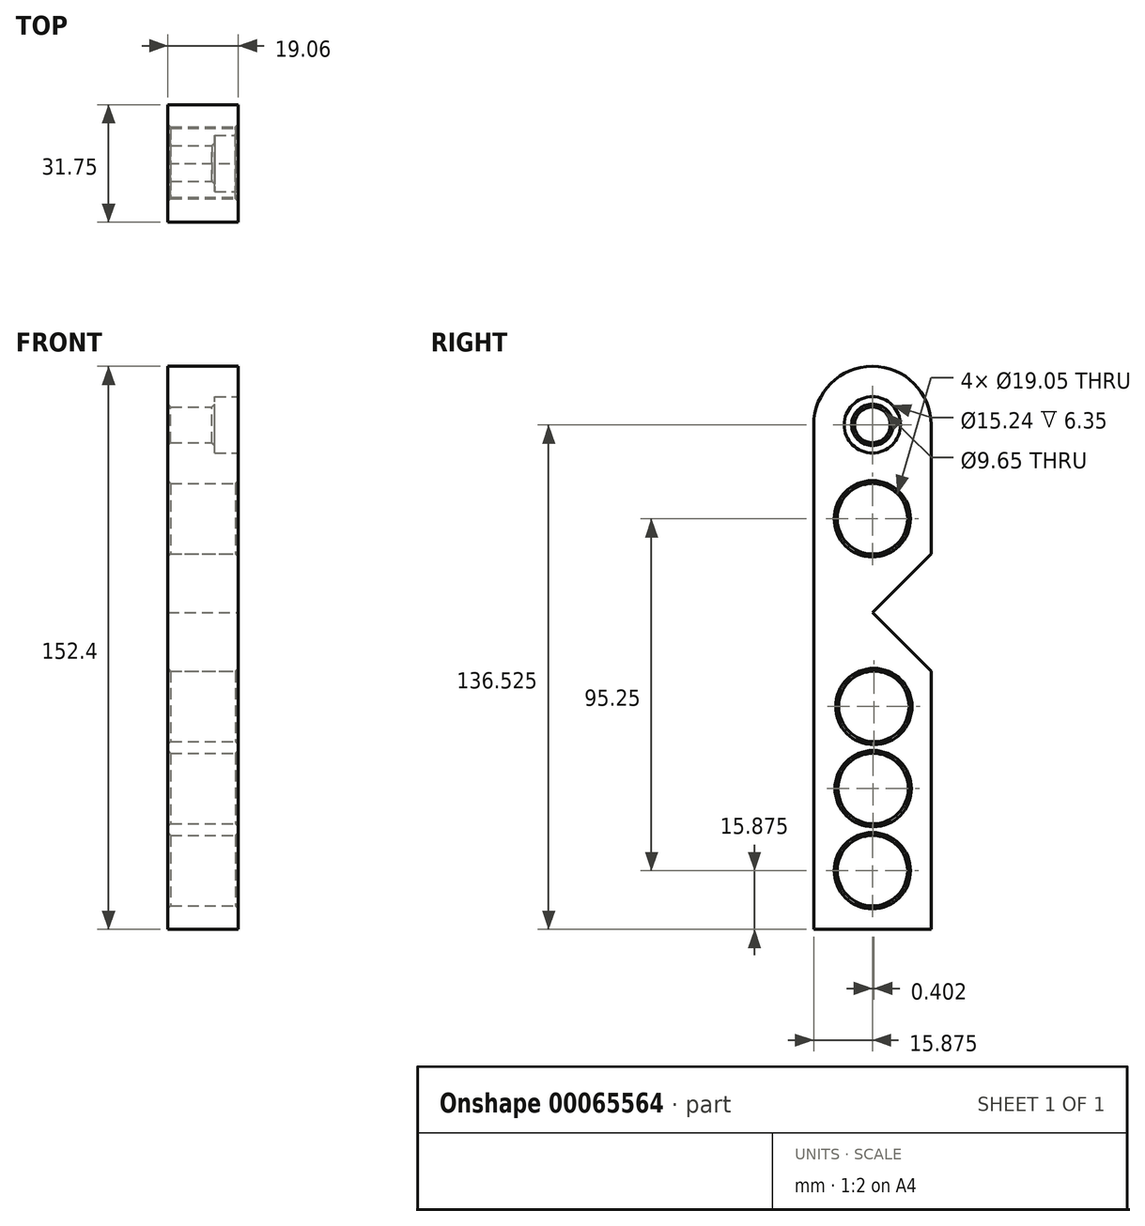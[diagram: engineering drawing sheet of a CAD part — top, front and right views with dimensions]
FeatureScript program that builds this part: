
annotation { "Feature Type Name" : "Feature", "Feature Type Description" : "" }
export const myFeature = defineFeature(function(context is Context, id is Id, definition is map)
    precondition{}
    {
        {
            var Q0;
            Q0=qCreatedBy(makeId("Front.planeOp"),FACE);
            var sketch = newSketch(context, id + "F0", { "sketchPlane" : qUnion([Q0])});
            skLineSegment(sketch, "E0.rect.bottom", {"start": v(-9.53, -76.2) * mm, "end": v(9.52, -76.2) * mm});
            skLineSegment(sketch, "E0.rect.top", {"start": v(-9.53, 76.2) * mm, "end": v(9.52, 76.2) * mm});
            skLineSegment(sketch, "E0.rect.left", {"start": v(-9.53, -76.2) * mm, "end": v(-9.53, 76.2) * mm});
            skLineSegment(sketch, "E0.rect.right", {"start": v(9.52, -76.2) * mm, "end": v(9.52, 76.2) * mm});
            skPoint(sketch, "E0.rect.middle", {"position": v(0, 0) * mm});
            skSolve(sketch);
        }
        {
            var Q0;
            Q0=makeQuery(id+"F0.imprint","IMPRINT",FACE,{"disambiguationData":[TD([[makeQuery(id+"F0.imprint","IMPRINT",EDGE,{"derivedFrom":sQuery(id+"F0.wireOp",EDGE,"E0.rect.bottom")}),1.0]])]});
            extrude(context, id + "F1", {"entities" : qUnion([Q0]), "depth" : 31.75 * mm});
        }
        {
            var Q0;
            Q0=makeQuery(id+"F1.opExtrude","SWEPT_FACE",FACE,{"disambiguationData":[OSD([sQuery(id+"F0.wireOp",EDGE,"E0.rect.right")])]});
            var sketch = newSketch(context, id + "F8", { "sketchPlane" : qUnion([Q0])});
            skCircle(sketch, "E1", {"center": v(-15.88, 60.33) * mm, "radius": 7.62 * mm});
            skCircle(sketch, "E2", {"center": v(-15.88, 60.33) * mm, "radius": 50.8 * mm, "construction": true});
            skLineSegment(sketch, "E3", {"start": v(-15.88, 60.33) * mm, "end": v(-15.88, -21.93) * mm, "construction": true});
            skLineSegment(sketch, "E4", {"start": v(-15.88, -21.93) * mm, "end": v(-15.88, 9.52) * mm, "construction": true});
            skLineSegment(sketch, "E5", {"start": v(-15.88, 9.52) * mm, "end": v(0, 9.52) * mm, "construction": true});
            skLineSegment(sketch, "E6", {"start": v(-15.88, 9.52) * mm, "end": v(0, 25.4) * mm});
            skLineSegment(sketch, "E7.MirrorCS", {"start": v(-15.87, 9.53) * mm, "end": v(0, -6.35) * mm});
            skCircle(sketch, "E8", {"center": v(-15.88, -60.33) * mm, "radius": 9.53 * mm});
            skPoint(sketch, "E8.centerSnap0", {"position": v(-15.88, -76.2) * mm});
            skCircle(sketch, "E9.1.0.0", {"center": v(-15.67, -38.1) * mm, "radius": 9.53 * mm});
            skCircle(sketch, "E9.2.0.0", {"center": v(-15.47, -15.88) * mm, "radius": 9.53 * mm});
            skLineSegment(sketch, "E9.direction1", {"start": v(-15.88, -60.33) * mm, "end": v(-15.67, -38.1) * mm, "construction": true});
            skCircle(sketch, "E10", {"center": v(-15.88, 34.92) * mm, "radius": 9.53 * mm});
            skSolve(sketch);
        }
        {
            var Q0;
            Q0=makeQuery(id+"F8.imprint","IMPRINT",FACE,{"disambiguationData":[TD([[makeQuery(id+"F8.imprint","IMPRINT",EDGE,{"derivedFrom":sQuery(id+"F8.wireOp",EDGE,"E1")}),1.0]])]});
            extrude(context, id + "F2", {"entities" : qUnion([Q0]), "operationType" : NewBodyOperationType.REMOVE, "oppositeDirection" : true, "depth" : 6.35 * mm});
        }
        {
            var Q0;
            Q0=makeQuery(id+"F2.boolean.opBoolean","COPY",FACE,{"derivedFrom":makeQuery(id+"F2.opExtrude","CAP_FACE",FACE,{"disambiguationData":[OSD([sQuery(id+"F8.wireOp",EDGE,"E1")])],"isStart":false})});
            var sketch = newSketch(context, id + "F3", { "sketchPlane" : qUnion([Q0])});
            skCircle(sketch, "E11", {"center": v(-15.88, 60.33) * mm, "radius": 4.83 * mm});
            skSolve(sketch);
        }
        {
            var Q0;
            Q0=makeQuery(id+"F3.imprint","IMPRINT",FACE,{"disambiguationData":[TD([[makeQuery(id+"F3.imprint","IMPRINT",EDGE,{"derivedFrom":sQuery(id+"F3.wireOp",EDGE,"E11")}),1.0]])]});
            extrude(context, id + "F9", {"entities" : qUnion([Q0]), "operationType" : NewBodyOperationType.REMOVE, "endBound" : BoundingType.UP_TO_NEXT, "oppositeDirection" : true, "depth" : 25.4 * mm});
        }
        {
            var Q0;
            Q0=makeQuery(id+"F1.opExtrude","CAP_EDGE",EDGE,{"disambiguationData":[OSD([sQuery(id+"F0.wireOp",EDGE,"E0.rect.top")])],"isStart":false});
            var Q1;
            Q1=makeQuery(id+"F1.opExtrude","CAP_EDGE",EDGE,{"disambiguationData":[OSD([sQuery(id+"F0.wireOp",EDGE,"E0.rect.top")])],"isStart":true});
            fillet(context, id + "F4", {"entities" : qUnion([Q0, Q1]), "radius" : 15.88 * mm, "tangentPropagation" : true, "allowEdgeOverflow" : false});
        }
        {
            var Q0;
            {var subQ0=sQuery(id+"F8.wireOp",EDGE,"E6");Q0=makeQuery(id+"F8.imprint","IMPRINT",FACE,{"disambiguationData":[TD([[makeQuery(id+"F8.imprint","IMPRINT",EDGE,{"derivedFrom":subQ0}),-1.0]])]});}
            extrude(context, id + "F5", {"entities" : qUnion([Q0]), "operationType" : NewBodyOperationType.REMOVE, "endBound" : BoundingType.UP_TO_NEXT, "oppositeDirection" : true, "depth" : 25.4 * mm});
        }
        {
            var Q0;
            Q0=makeQuery(id+"F8.imprint","IMPRINT",FACE,{"disambiguationData":[TD([[makeQuery(id+"F8.imprint","IMPRINT",EDGE,{"derivedFrom":sQuery(id+"F8.wireOp",EDGE,"E10")}),1.0]])]});
            var Q1;
            Q1=makeQuery(id+"F8.imprint","IMPRINT",FACE,{"disambiguationData":[TD([[makeQuery(id+"F8.imprint","IMPRINT",EDGE,{"derivedFrom":sQuery(id+"F8.wireOp",EDGE,"E9.2.0.0")}),1.0]])]});
            var Q2;
            Q2=makeQuery(id+"F8.imprint","IMPRINT",FACE,{"disambiguationData":[TD([[makeQuery(id+"F8.imprint","IMPRINT",EDGE,{"derivedFrom":sQuery(id+"F8.wireOp",EDGE,"E9.1.0.0")}),1.0]])]});
            var Q3;
            Q3=makeQuery(id+"F8.imprint","IMPRINT",FACE,{"disambiguationData":[TD([[makeQuery(id+"F8.imprint","IMPRINT",EDGE,{"derivedFrom":sQuery(id+"F8.wireOp",EDGE,"E8")}),1.0]])]});
            extrude(context, id + "F6", {"entities" : qUnion([Q0, Q1, Q2, Q3]), "operationType" : NewBodyOperationType.REMOVE, "endBound" : BoundingType.UP_TO_NEXT, "oppositeDirection" : true, "depth" : 25.4 * mm});
        }
        {
            var Q0;
            Q0=makeQuery(id+"F6.boolean.opBoolean","COPY",FACE,{"derivedFrom":makeQuery(id+"F6.opExtrude","SWEPT_FACE",FACE,{"disambiguationData":[OSD([sQuery(id+"F8.wireOp",EDGE,"E10")])]})});
            var Q1;
            Q1=makeQuery(id+"F6.boolean.opBoolean","COPY",FACE,{"derivedFrom":makeQuery(id+"F6.opExtrude","SWEPT_FACE",FACE,{"disambiguationData":[OSD([sQuery(id+"F8.wireOp",EDGE,"E9.2.0.0")])]})});
            var Q2;
            Q2=makeQuery(id+"F6.boolean.opBoolean","COPY",FACE,{"derivedFrom":makeQuery(id+"F6.opExtrude","SWEPT_FACE",FACE,{"disambiguationData":[OSD([sQuery(id+"F8.wireOp",EDGE,"E9.1.0.0")])]})});
            var Q3;
            Q3=makeQuery(id+"F6.boolean.opBoolean","COPY",FACE,{"derivedFrom":makeQuery(id+"F6.opExtrude","SWEPT_FACE",FACE,{"disambiguationData":[OSD([sQuery(id+"F8.wireOp",EDGE,"E8")])]})});
            var Q4;
            Q4=makeQuery(id+"F2.boolean.opBoolean","COPY",EDGE,{"derivedFrom":makeQuery(id+"F2.opExtrude","CAP_EDGE",EDGE,{"disambiguationData":[OSD([sQuery(id+"F8.wireOp",EDGE,"E1")])],"isStart":true})});
            var Q5;
            Q5=makeQuery(id+"F9.boolean.opBoolean","COPY",FACE,{"derivedFrom":makeQuery(id+"F9.opExtrude","SWEPT_FACE",FACE,{"disambiguationData":[OSD([sQuery(id+"F3.wireOp",EDGE,"E11")])]})});
            chamfer(context, id + "F7", {"entities" : qUnion([Q0, Q1, Q2, Q3, Q4, Q5]), "width" : 0.8 * mm, "tangentPropagation" : true});
        }
    });
